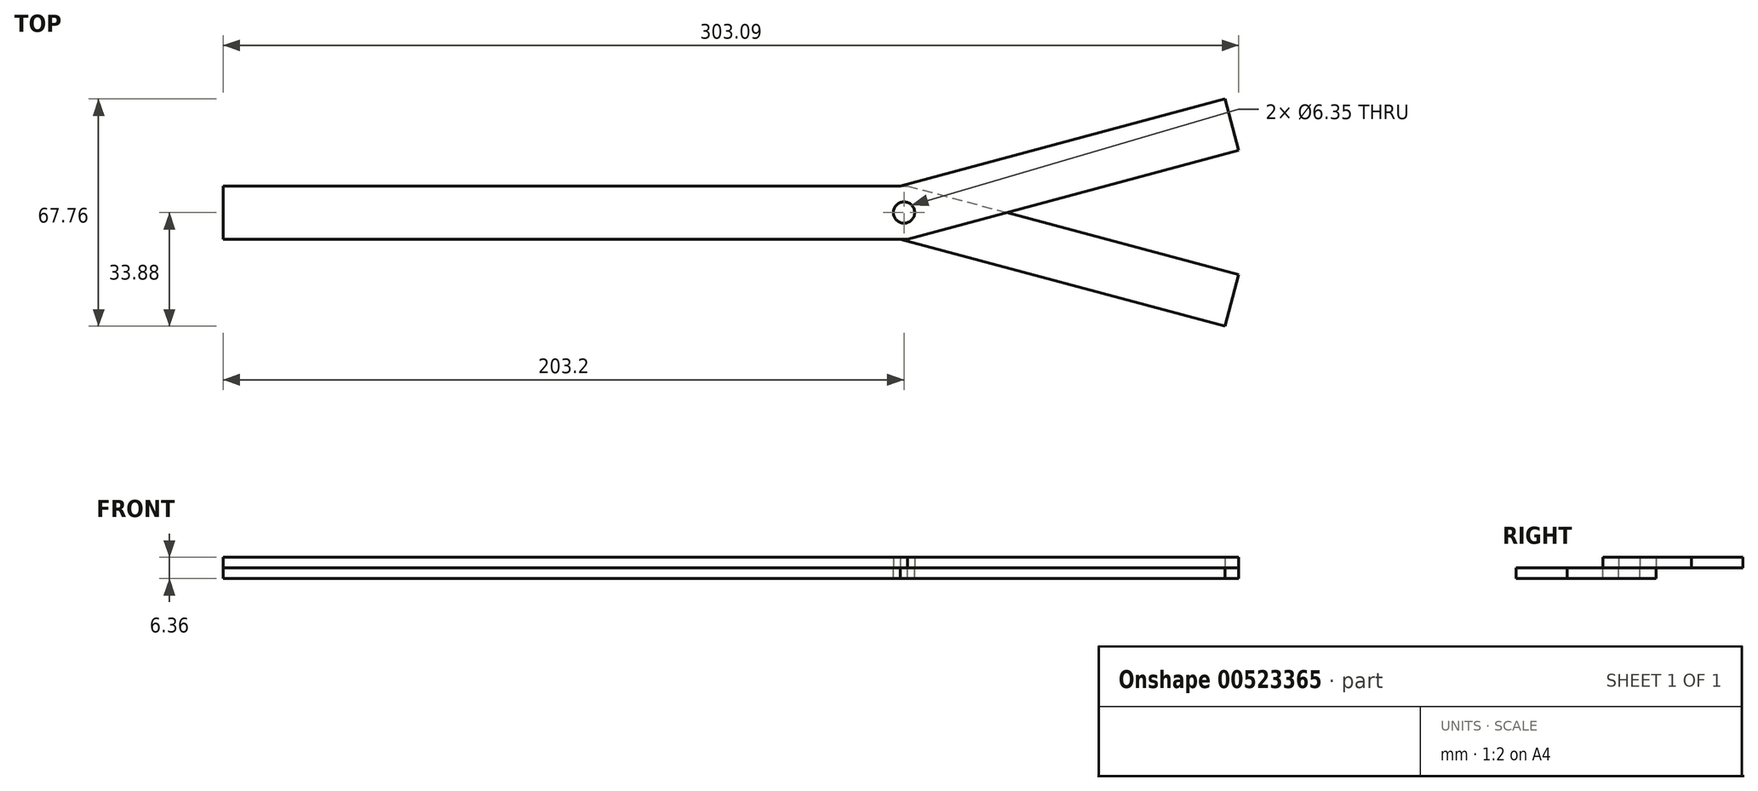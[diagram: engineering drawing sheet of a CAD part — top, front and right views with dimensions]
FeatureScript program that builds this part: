
annotation { "Feature Type Name" : "Feature", "Feature Type Description" : "" }
export const myFeature = defineFeature(function(context is Context, id is Id, definition is map)
    precondition{}
    {
        {
            var Q0;
            Q0=qCreatedBy(makeId("Top.planeOp"),FACE);
            var sketch = newSketch(context, id + "F0", { "sketchPlane" : qUnion([Q0])});
            skLineSegment(sketch, "E0", {"start": v(-203.2, -7.94) * mm, "end": v(1.04, -7.94) * mm});
            skLineSegment(sketch, "E1", {"start": v(1.04, -7.94) * mm, "end": v(99.9, 18.55) * mm});
            skLineSegment(sketch, "E2", {"start": v(99.9, 18.55) * mm, "end": v(95.78, 33.88) * mm});
            skLineSegment(sketch, "E3", {"start": v(95.78, 33.88) * mm, "end": v(-1.04, 7.94) * mm});
            skLineSegment(sketch, "E4", {"start": v(-1.04, 7.94) * mm, "end": v(-203.2, 7.94) * mm});
            skLineSegment(sketch, "E5", {"start": v(-203.2, 7.94) * mm, "end": v(-203.2, -7.94) * mm});
            skLineSegment(sketch, "E6", {"start": v(-1.04, 7.94) * mm, "end": v(1.04, -7.94) * mm, "construction": true});
            skPoint(sketch, "E7", {"position": v(0, 0) * mm});
            skCircle(sketch, "E8", {"center": v(0, 0) * mm, "radius": 3.18 * mm});
            skLineSegment(sketch, "E9.MirrorCS", {"start": v(1.04, 7.94) * mm, "end": v(99.9, -18.55) * mm});
            skLineSegment(sketch, "E10.MirrorCS", {"start": v(99.9, -18.55) * mm, "end": v(95.78, -33.88) * mm});
            skLineSegment(sketch, "E11.MirrorCS", {"start": v(95.78, -33.88) * mm, "end": v(-1.04, -7.94) * mm});
            skLineSegment(sketch, "E12.MirrorCS", {"start": v(-1.04, -7.94) * mm, "end": v(-203.2, -7.94) * mm});
            skLineSegment(sketch, "E13.MirrorCS", {"start": v(-203.2, 7.94) * mm, "end": v(1.04, 7.94) * mm});
            skSolve(sketch);
        }
        {
            var Q0;
            {var subQ1=sQuery(id+"F0.wireOp",EDGE,"E0");Q0=makeQuery(id+"F0.imprint","IMPRINT",FACE,{"disambiguationData":[TD([[makeQuery(id+"F0.imprint","IMPRINT",EDGE,{"derivedFrom":subQ1}),1.0]])]});}
            var Q1;
            {var subQ1=sQuery(id+"F0.wireOp",EDGE,"E2");Q1=makeQuery(id+"F0.imprint","IMPRINT",FACE,{"disambiguationData":[TD([[makeQuery(id+"F0.imprint","IMPRINT",EDGE,{"derivedFrom":subQ1}),1.0]])]});}
            extrude(context, id + "F1", {"entities" : qUnion([Q0, Q1]), "depth" : 3.17 * mm, "offsetDistance" : 25.4 * mm});
        }
        {
            var Q0;
            {var subQ4=sQuery(id+"F0.wireOp",EDGE,"E0");Q0=makeQuery(id+"F0.imprint","IMPRINT",FACE,{"disambiguationData":[TD([[makeQuery(id+"F0.imprint","IMPRINT",EDGE,{"derivedFrom":subQ4}),-1.0]])]});}
            var Q1;
            {var subQ1=sQuery(id+"F0.wireOp",EDGE,"E0");Q1=makeQuery(id+"F0.imprint","IMPRINT",FACE,{"disambiguationData":[TD([[makeQuery(id+"F0.imprint","IMPRINT",EDGE,{"derivedFrom":subQ1}),1.0]])]});}
            extrude(context, id + "F2", {"entities" : qUnion([Q0, Q1]), "oppositeDirection" : true, "depth" : 3.17 * mm, "offsetDistance" : 25.4 * mm});
        }
    });
